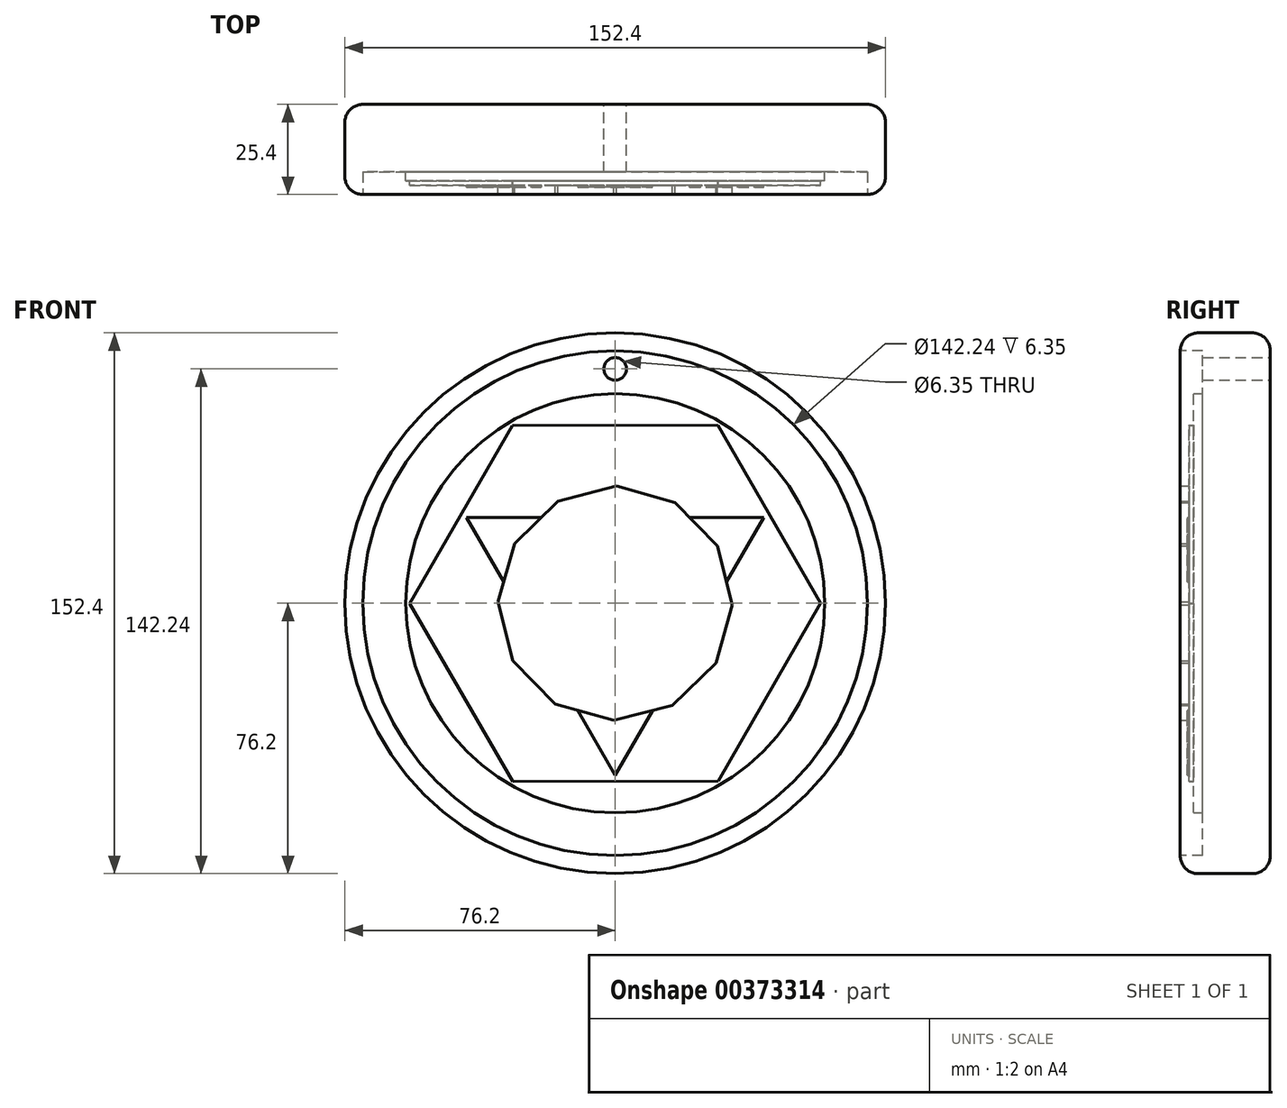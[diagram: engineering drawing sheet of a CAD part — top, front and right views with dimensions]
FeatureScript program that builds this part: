
annotation { "Feature Type Name" : "Feature", "Feature Type Description" : "" }
export const myFeature = defineFeature(function(context is Context, id is Id, definition is map)
    precondition{}
    {
        {
            var Q0;
            Q0=qCreatedBy(makeId("Front.planeOp"),FACE);
            var sketch = newSketch(context, id + "F0", { "sketchPlane" : qUnion([Q0])});
            skCircle(sketch, "E0", {"center": v(0, 0) * mm, "radius": 76.2 * mm});
            skSolve(sketch);
        }
        {
            var Q0;
            Q0=makeQuery(id+"F0.imprint","IMPRINT",FACE,{"disambiguationData":[TD([[makeQuery(id+"F0.imprint","IMPRINT",EDGE,{"derivedFrom":sQuery(id+"F0.wireOp",EDGE,"E0")}),1.0]])]});
            extrude(context, id + "F1", {"entities" : qUnion([Q0]), "depth" : 25.4 * mm});
        }
        {
            var Q0;
            Q0=makeQuery(id+"F1.opExtrude","SWEPT_FACE",FACE,{"disambiguationData":[OSD([sQuery(id+"F0.wireOp",EDGE,"E0")])]});
            fillet(context, id + "F2", {"entities" : qUnion([Q0]), "radius" : 5.08 * mm, "tangentPropagation" : true, "allowEdgeOverflow" : false});
        }
        {
            var Q0;
            Q0=makeQuery(id+"F1.opExtrude","CAP_FACE",FACE,{"disambiguationData":[OSD([sQuery(id+"F0.wireOp",EDGE,"E0")])],"isStart":false});
            extrude(context, id + "F3", {"entities" : qUnion([Q0]), "operationType" : NewBodyOperationType.REMOVE, "oppositeDirection" : true, "depth" : 6.35 * mm});
        }
        {
            var Q0;
            Q0=qCreatedBy(makeId("Front.planeOp"),FACE);
            var sketch = newSketch(context, id + "F4", { "sketchPlane" : qUnion([Q0])});
            skCircle(sketch, "E1", {"center": v(0, 66.04) * mm, "radius": 3.18 * mm});
            skSolve(sketch);
        }
        {
            var Q0;
            Q0=makeQuery(id+"F4.imprint","IMPRINT",FACE,{"disambiguationData":[TD([[makeQuery(id+"F4.imprint","IMPRINT",EDGE,{"derivedFrom":sQuery(id+"F4.wireOp",EDGE,"E1")}),1.0]])]});
            var Q1;
            Q1=sQuery(id+"F4.wireOp",EDGE,"E1");
            extrude(context, id + "F5", {"entities" : qUnion([Q0]), "operationType" : NewBodyOperationType.REMOVE, "surfaceEntities" : qUnion([Q1]), "depth" : 25.4 * mm});
        }
        {
            var Q0;
            Q0=qCreatedBy(makeId("Front.planeOp"),FACE);
            var sketch = newSketch(context, id + "F6", { "sketchPlane" : qUnion([Q0])});
            skCircle(sketch, "E2", {"center": v(0, 0) * mm, "radius": 59.06 * mm});
            skSolve(sketch);
        }
        {
            var Q0;
            Q0 = qSketchRegion(id + "F6", true);
            extrude(context, id + "F7", {"entities" : qUnion([Q0]), "operationType" : NewBodyOperationType.ADD, "depth" : 21.59 * mm});
        }
        {
            var Q0;
            Q0=qCreatedBy(makeId("Front.planeOp"),FACE);
            var sketch = newSketch(context, id + "F8", { "sketchPlane" : qUnion([Q0])});
            skCircle(sketch, "E3.cCircle", {"center": v(0, 0) * mm, "radius": 50.18 * mm, "construction": true});
            skLineSegment(sketch, "E3.0", {"start": v(57.95, 0.07) * mm, "end": v(29.04, -50.15) * mm});
            skLineSegment(sketch, "E3.1", {"start": v(29.04, -50.15) * mm, "end": v(-28.9, -50.22) * mm});
            skLineSegment(sketch, "E3.2", {"start": v(-28.9, -50.22) * mm, "end": v(-57.95, -0.07) * mm});
            skLineSegment(sketch, "E3.3", {"start": v(-57.95, -0.07) * mm, "end": v(-29.04, 50.15) * mm});
            skLineSegment(sketch, "E3.4", {"start": v(-29.04, 50.15) * mm, "end": v(28.9, 50.22) * mm});
            skLineSegment(sketch, "E3.5", {"start": v(28.9, 50.22) * mm, "end": v(57.95, 0.07) * mm});
            skPoint(sketch, "E3.0.midPoint", {"position": v(43.5, -25.04) * mm});
            skSolve(sketch);
        }
        {
            var Q0;
            Q0=makeQuery(id+"F8.imprint","IMPRINT",FACE,{"disambiguationData":[TD([[makeQuery(id+"F8.imprint","IMPRINT",EDGE,{"derivedFrom":sQuery(id+"F8.wireOp",EDGE,"E3.0")}),-1.0]])]});
            extrude(context, id + "F9", {"entities" : qUnion([Q0]), "operationType" : NewBodyOperationType.ADD, "depth" : 22.86 * mm});
        }
        {
            var Q0;
            Q0=qCreatedBy(makeId("Front.planeOp"),FACE);
            var sketch = newSketch(context, id + "F10", { "sketchPlane" : qUnion([Q0])});
            skCircle(sketch, "E4.cCircle", {"center": v(0, 0) * mm, "radius": 48.4 * mm, "construction": true});
            skLineSegment(sketch, "E4.0", {"start": v(0, -48.4) * mm, "end": v(-41.92, 24.2) * mm});
            skLineSegment(sketch, "E4.1", {"start": v(-41.92, 24.2) * mm, "end": v(41.92, 24.2) * mm});
            skLineSegment(sketch, "E4.2", {"start": v(41.92, 24.2) * mm, "end": v(0, -48.4) * mm});
            skSolve(sketch);
        }
        {
            var Q0;
            Q0=makeQuery(id+"F10.imprint","IMPRINT",FACE,{"disambiguationData":[TD([[makeQuery(id+"F10.imprint","IMPRINT",EDGE,{"derivedFrom":sQuery(id+"F10.wireOp",EDGE,"E4.0")}),-1.0]])]});
            extrude(context, id + "F11", {"entities" : qUnion([Q0]), "operationType" : NewBodyOperationType.ADD, "depth" : 23.37 * mm});
        }
        {
            var Q0;
            Q0=qCreatedBy(makeId("Front.planeOp"),FACE);
            var sketch = newSketch(context, id + "F12", { "sketchPlane" : qUnion([Q0])});
            skCircle(sketch, "E5.cCircle", {"center": v(0, 0) * mm, "radius": 33.02 * mm, "construction": true});
            skLineSegment(sketch, "E5.0", {"start": v(28.8, 16.16) * mm, "end": v(33.02, -0.4) * mm});
            skLineSegment(sketch, "E5.1", {"start": v(33.02, -0.4) * mm, "end": v(28.4, -16.86) * mm});
            skLineSegment(sketch, "E5.2", {"start": v(28.4, -16.86) * mm, "end": v(16.16, -28.8) * mm});
            skLineSegment(sketch, "E5.3", {"start": v(16.16, -28.8) * mm, "end": v(-0.4, -33.02) * mm});
            skLineSegment(sketch, "E5.4", {"start": v(-0.4, -33.02) * mm, "end": v(-16.86, -28.4) * mm});
            skLineSegment(sketch, "E5.5", {"start": v(-16.86, -28.4) * mm, "end": v(-28.8, -16.16) * mm});
            skLineSegment(sketch, "E5.6", {"start": v(-28.8, -16.16) * mm, "end": v(-33.02, 0.4) * mm});
            skLineSegment(sketch, "E5.7", {"start": v(-33.02, 0.4) * mm, "end": v(-28.4, 16.86) * mm});
            skLineSegment(sketch, "E5.8", {"start": v(-28.4, 16.86) * mm, "end": v(-16.16, 28.8) * mm});
            skLineSegment(sketch, "E5.9", {"start": v(-16.16, 28.8) * mm, "end": v(0.4, 33.02) * mm});
            skLineSegment(sketch, "E5.10", {"start": v(0.4, 33.02) * mm, "end": v(16.86, 28.4) * mm});
            skLineSegment(sketch, "E5.11", {"start": v(16.86, 28.4) * mm, "end": v(28.8, 16.16) * mm});
            skSolve(sketch);
        }
        {
            var Q0;
            Q0=makeQuery(id+"F12.imprint","IMPRINT",FACE,{"disambiguationData":[TD([[makeQuery(id+"F12.imprint","IMPRINT",EDGE,{"derivedFrom":sQuery(id+"F12.wireOp",EDGE,"E5.0")}),-1.0]])]});
            extrude(context, id + "F13", {"entities" : qUnion([Q0]), "operationType" : NewBodyOperationType.ADD, "depth" : 25.4 * mm});
        }
    });
